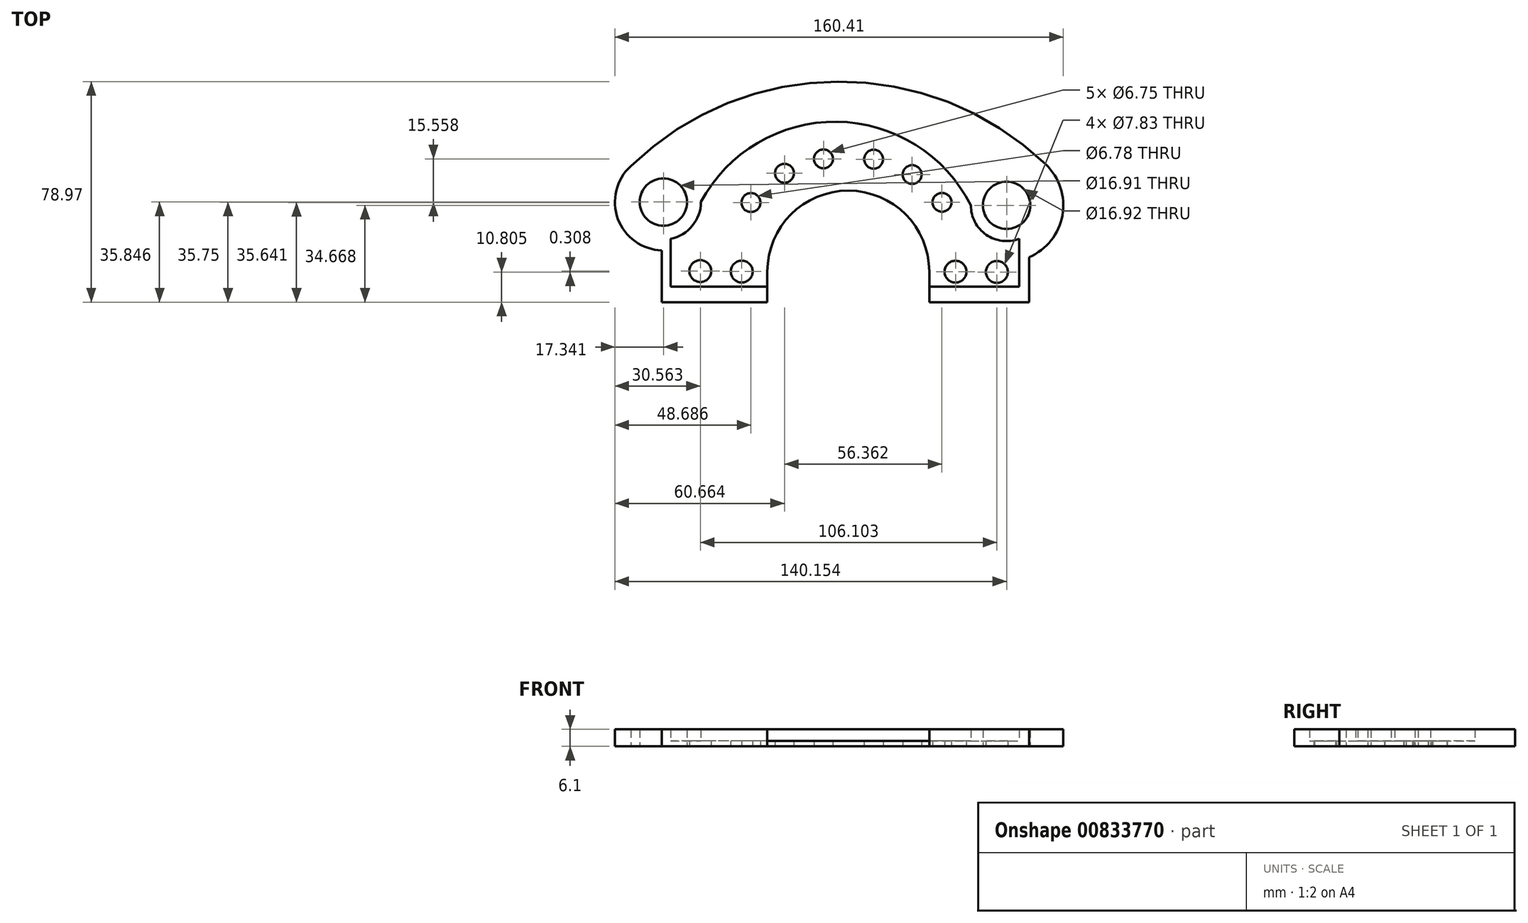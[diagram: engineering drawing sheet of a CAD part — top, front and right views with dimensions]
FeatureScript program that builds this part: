
annotation { "Feature Type Name" : "Feature", "Feature Type Description" : "" }
export const myFeature = defineFeature(function(context is Context, id is Id, definition is map)
    precondition{}
    {
        {
            var Q0;
            Q0=qCreatedBy(makeId("Top.planeOp"),FACE);
            var sketch = newSketch(context, id + "F0", { "sketchPlane" : qUnion([Q0])});
            skArc(sketch, "E0", {"start": v(36.67, 99.22) * mm, "mid": v(-37.7, 128.88) * mm, "end": v(-111.82, 98.58) * mm});
            skArc(sketch, "E1", {"start": v(36.67, 99.22) * mm, "mid": v(42.61, 81.03) * mm, "end": v(30.77, 66.01) * mm});
            skArc(sketch, "E2", {"start": v(-100.7, 68.42) * mm, "mid": v(-116.42, 79.76) * mm, "end": v(-111.82, 98.58) * mm});
            skLineSegment(sketch, "E3", {"start": v(-100.7, 68.42) * mm, "end": v(-100.7, 49.91) * mm});
            skLineSegment(sketch, "E4", {"start": v(30.77, 49.91) * mm, "end": v(30.77, 66.01) * mm});
            skLineSegment(sketch, "E5", {"start": v(-100.7, 49.91) * mm, "end": v(-62.96, 49.91) * mm});
            skLineSegment(sketch, "E6", {"start": v(30.77, 49.91) * mm, "end": v(-5.02, 49.91) * mm});
            skLineSegment(sketch, "E7", {"start": v(-5.02, 49.91) * mm, "end": v(-5.02, 60.86) * mm});
            skLineSegment(sketch, "E8", {"start": v(-62.96, 49.91) * mm, "end": v(-62.96, 60.86) * mm});
            skArc(sketch, "E9", {"start": v(-5.02, 60.86) * mm, "mid": v(-33.99, 89.83) * mm, "end": v(-62.96, 60.86) * mm});
            skLineSegment(sketch, "E10", {"start": v(-62.96, 55.39) * mm, "end": v(-82.53, 55.39) * mm});
            skLineSegment(sketch, "E11", {"start": v(-82.53, 55.39) * mm, "end": v(-97.56, 55.39) * mm});
            skLineSegment(sketch, "E12", {"start": v(-5.02, 55.39) * mm, "end": v(27.16, 55.39) * mm});
            skCircle(sketch, "E13", {"center": v(-72.12, 60.86) * mm, "radius": 3.91 * mm});
            skCircle(sketch, "E14", {"center": v(-72.12, 60.86) * mm, "radius": 2.35 * mm});
            skCircle(sketch, "E15", {"center": v(-86.93, 61.02) * mm, "radius": 3.91 * mm});
            skCircle(sketch, "E16", {"center": v(-86.93, 61.02) * mm, "radius": 2.35 * mm});
            skCircle(sketch, "E17", {"center": v(4.37, 60.8) * mm, "radius": 3.91 * mm});
            skCircle(sketch, "E18", {"center": v(19.18, 60.72) * mm, "radius": 3.91 * mm});
            skCircle(sketch, "E19", {"center": v(19.18, 60.72) * mm, "radius": 2.35 * mm});
            skCircle(sketch, "E20", {"center": v(4.37, 60.88) * mm, "radius": 2.35 * mm});
            skCircle(sketch, "E21", {"center": v(-68.8, 85.55) * mm, "radius": 3.39 * mm});
            skCircle(sketch, "E22", {"center": v(-0.46, 85.66) * mm, "radius": 3.38 * mm});
            skCircle(sketch, "E23", {"center": v(-56.83, 96.07) * mm, "radius": 3.38 * mm});
            skCircle(sketch, "E24", {"center": v(-42.87, 101.22) * mm, "radius": 3.38 * mm});
            skCircle(sketch, "E25", {"center": v(-24.91, 101.1) * mm, "radius": 3.38 * mm});
            skCircle(sketch, "E26", {"center": v(-11.15, 95.58) * mm, "radius": 3.38 * mm});
            skLineSegment(sketch, "E27", {"start": v(-97.56, 55.39) * mm, "end": v(-97.56, 72.6) * mm});
            skLineSegment(sketch, "E28", {"start": v(27.16, 55.39) * mm, "end": v(27.16, 72.6) * mm});
            skArc(sketch, "E29", {"start": v(27.16, 72.6) * mm, "mid": v(15.37, 74.05) * mm, "end": v(9.86, 84.58) * mm});
            skArc(sketch, "E30", {"start": v(-97.56, 72.6) * mm, "mid": v(-89.79, 77.23) * mm, "end": v(-86.73, 85.76) * mm});
            skArc(sketch, "E31", {"start": v(9.86, 84.58) * mm, "mid": v(-38.08, 114.5) * mm, "end": v(-86.73, 85.76) * mm});
            skCircle(sketch, "E32", {"center": v(-100.15, 85.76) * mm, "radius": 8.45 * mm});
            skCircle(sketch, "E33", {"center": v(22.66, 84.58) * mm, "radius": 8.46 * mm});
            skSolve(sketch);
        }
        {
            var Q0;
            {var subQ1=sQuery(id+"F0.wireOp",EDGE,"E9");Q0=makeQuery(id+"F0.imprint","IMPRINT",FACE,{"disambiguationData":[TD([[makeQuery(id+"F0.imprint","IMPRINT",EDGE,{"derivedFrom":subQ1}),-1.0]])]});}
            extrude(context, id + "F1", {"entities" : qUnion([Q0]), "depth" : 2 * mm, "offsetDistance" : 25.4 * mm});
        }
        {
            var Q0;
            Q0=sQuery(id+"F0.wireOp",EDGE,"E19");
            var Q1;
            Q1=sQuery(id+"F0.wireOp",EDGE,"E20");
            var Q2;
            Q2=sQuery(id+"F0.wireOp",EDGE,"E14");
            var Q3;
            Q3=sQuery(id+"F0.wireOp",EDGE,"E16");
            extrude(context, id + "F2", {"bodyType" : ToolBodyType.SURFACE, "surfaceEntities" : qUnion([Q0, Q1, Q2, Q3]), "depth" : 2.5 * mm, "offsetDistance" : 25.4 * mm});
        }
        {
            var Q0;
            Q0=sQuery(id+"F0.wireOp",EDGE,"E30");
            var Q1;
            Q1=sQuery(id+"F0.wireOp",EDGE,"E31");
            var Q2;
            Q2=sQuery(id+"F0.wireOp",EDGE,"E29");
            var Q3;
            Q3=sQuery(id+"F0.wireOp",EDGE,"E28");
            var Q4;
            Q4=sQuery(id+"F0.wireOp",EDGE,"E12");
            var Q5;
            Q5=sQuery(id+"F0.wireOp",EDGE,"E10");
            var Q6;
            Q6=sQuery(id+"F0.wireOp",EDGE,"E11");
            var Q7;
            Q7=sQuery(id+"F0.wireOp",EDGE,"E27");
            extrude(context, id + "F3", {"bodyType" : ToolBodyType.SURFACE, "surfaceEntities" : qUnion([Q0, Q1, Q2, Q3, Q4, Q5, Q6, Q7]), "depth" : 3.5 * mm, "offsetDistance" : 25.4 * mm});
        }
        {
            var Q0;
            Q0=sQuery(id+"F0.wireOp",EDGE,"E8");
            var Q1;
            Q1=sQuery(id+"F0.wireOp",EDGE,"E9");
            var Q2;
            Q2=sQuery(id+"F0.wireOp",EDGE,"E7");
            var Q3;
            Q3=sQuery(id+"F0.wireOp",EDGE,"E4");
            var Q4;
            Q4=sQuery(id+"F0.wireOp",EDGE,"E1");
            var Q5;
            Q5=sQuery(id+"F0.wireOp",EDGE,"E0");
            var Q6;
            Q6=sQuery(id+"F0.wireOp",EDGE,"E2");
            var Q7;
            Q7=sQuery(id+"F0.wireOp",EDGE,"E3");
            var Q8;
            Q8=sQuery(id+"F0.wireOp",EDGE,"E5");
            var Q9;
            Q9=sQuery(id+"F0.wireOp",EDGE,"E6");
            extrude(context, id + "F4", {"bodyType" : ToolBodyType.SURFACE, "surfaceEntities" : qUnion([Q0, Q1, Q2, Q3, Q4, Q5, Q6, Q7, Q8, Q9]), "depth" : 5.5 * mm, "offsetDistance" : 25.4 * mm});
        }
        {
            var Q0;
            Q0=makeQuery(id+"F0.imprint","IMPRINT",FACE,{"disambiguationData":[TD([[makeQuery(id+"F0.imprint","IMPRINT",EDGE,{"derivedFrom":sQuery(id+"F0.wireOp",EDGE,"E0")}),1.0]])]});
            extrude(context, id + "F5", {"entities" : qUnion([Q0]), "operationType" : NewBodyOperationType.ADD, "depth" : 6 * mm, "offsetDistance" : 25.4 * mm});
        }
        {
            var Q0;
            Q0=makeQuery(id+"F0.imprint","IMPRINT",FACE,{"disambiguationData":[TD([[makeQuery(id+"F0.imprint","IMPRINT",EDGE,{"derivedFrom":sQuery(id+"F0.wireOp",EDGE,"E0")}),1.0]])]});
            extrude(context, id + "F6", {"entities" : qUnion([Q0]), "operationType" : NewBodyOperationType.ADD, "depth" : 6 * mm, "offsetDistance" : 25.4 * mm});
        }
        {
            var Q0;
            Q0=makeQuery(id+"F0.imprint","IMPRINT",FACE,{"disambiguationData":[TD([[makeQuery(id+"F0.imprint","IMPRINT",EDGE,{"derivedFrom":sQuery(id+"F0.wireOp",EDGE,"E0")}),1.0]])]});
            extrude(context, id + "F7", {"entities" : qUnion([Q0]), "operationType" : NewBodyOperationType.ADD, "depth" : 6.1 * mm, "offsetDistance" : 25.4 * mm});
        }
    });
